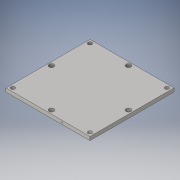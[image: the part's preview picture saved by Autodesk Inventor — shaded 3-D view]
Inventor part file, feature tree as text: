
AUTODESK INVENTOR PART (.ipt)
format: ipt  version: 2016 (Build 200138000, 138)  size: 120,320 bytes
history: native  units: in
note: dims shown in document units (in); Inventor stores cm internally (conversion verified against a paired STEP export)
features: extrude x2, sketch x2
ambient origin geometry x8: Origin, YZ Plane, XZ Plane, XY Plane, X Axis, Y Axis, Z Axis, Center Point
bodies: Solid1 (feature_tree)
feature tree (4):
  extrude  "Extrusion1"  Depth=3.0in
  extrude  "Extrusion2"  Depth=0.5in
  sketch  "Sketch1"  dims[d0=3.0in d1=3.0in]
  sketch  "Sketch2"  dims[d2=0.125in d3=0.172in d4=0.125in d5=0.125in d6=0.125in d7=0.172in d8=0.172in d9=0.172in d10=0.14in d11=0.14in d12=0.14in d13=0.14in d14=0.13in d15=0.0in d17=0.04in d18=0.5in d19=0.0in]
